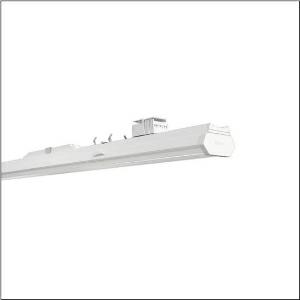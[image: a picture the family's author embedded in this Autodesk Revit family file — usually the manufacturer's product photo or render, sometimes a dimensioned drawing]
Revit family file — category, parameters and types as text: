
# Revit family: licross_11_protected_mo_51tp11cn49xg
name_source: partatom
category: Lighting Fixtures
units: mm (PartAtom-declared; Revit-internal decimal feet)

## family parameters
Cut with Voids When Loaded = No
Host = Face
Light Source = No
Part Type = Normal
Room Calculation Point = No
Round Connector Dimension = Use Diameter
Shared = No

## types (1)
- --- (1 x LED, 9030 lm, 49.4 W, 4000K)
    Apparent Load = 49 VA
    CIE Flux Codes = 83 94 98 100 100
    Color Rendering = 80
    Color Temperature = 4000K
    Default Elevation = 1800 mm
    Description = Licross 11 Protected MO, luminaire insert, of sheet steel, galvanised, coil coated, white, length: 1.500mm, width: 90mm, height: 101mm, LED rated luminous flux: 9.030lm, light colour: 840, SDCM (Standard Deviation of Colour Matching)MacAdam ≤ 2 SDCM (initial), control gear: ON/OFF Multilumen, CLOi, with plug, 3-pole, with phase selection, mains connection: 220..240V, AC, 50/60Hz, start of lifetime: 49W, end of service life: 55W, internal wiring halogen-free, primary light control with lens, of plastic, primary optical cover: cover, of PMMA, light emission: direct distribution, primary light characteristic: symmetric, protection rating (complete): IP64, insulation class (complete): insulation class I (protective earthing), certification: CE, ENEC, VDE, UKCA, protection symbol: D if used in an environment with conductive dust loads with corresponding accessories, impact resistance: IK06, permissible ambient temperature for indoor applications: -35..+40°C, corresponds to IFS (International Featured Standards) requirements for safety and quality in the food industry, reducing of maximum allowable ambient temperature of 5°C with ceiling mounting, LABS conformity tested according to VDMA 24364:2018-05, The light source and the operating device comply with the requirements of the Ecodesign Regulation (EU) 2019/2020 and are replaceable in accordance with this regulation, packaging unit: 1 piece
    Height = 92 mm
    Lamp = 1 x LED
    Lamp Light Flux = 9030 lm
    Lamp Power = 49.4 W
    Lamp count = 1
    Length = 1500 mm
    Luminous efficacy = 183 lm/W
    Manufacturer = Siteco
    ModVariant = No
    Model = 51TP11CN49XG
    Mounting Place = Ceiling
    Mounting Type = Pendant
    Number of Poles = 1
    OnlyDefault = Yes
    Power Factor = 1
    Product Name = Licross 11 Protected MO
    Product group = luminaire insert | ceiling pendant
    ProductGroupID = 901
    Protection Class = Protection class I
    Protection Degree = IP 64
    RLX_Detail_Level = 1
    RLX_Emergency_Light_Flux = 0 lm
    RLX_Emergency_Type = 0
    RLX_Emergency_Type_DB = No
    RlxData = <blob elided: 22109 chars, md5=baae9bdc>
    Socket = socket
    Standby Power = 0 W
    System Light Flux = 9030 lm
    System Power = 49 W
    Type Comments = factory setting: luminous flux: 100 % | (A | C | E) | 113 mA
    Type Image = l_1256148.jpg
    URL = http://relux.com
    VarID = @adj_091085
    Voltage = 0 V
    Weight = 0.00 kg
    Width = 88 mm

## geometry (parser evidence)
native form markers: Blend x4, Sweep x10
no freeform markers — native parametric forms only
